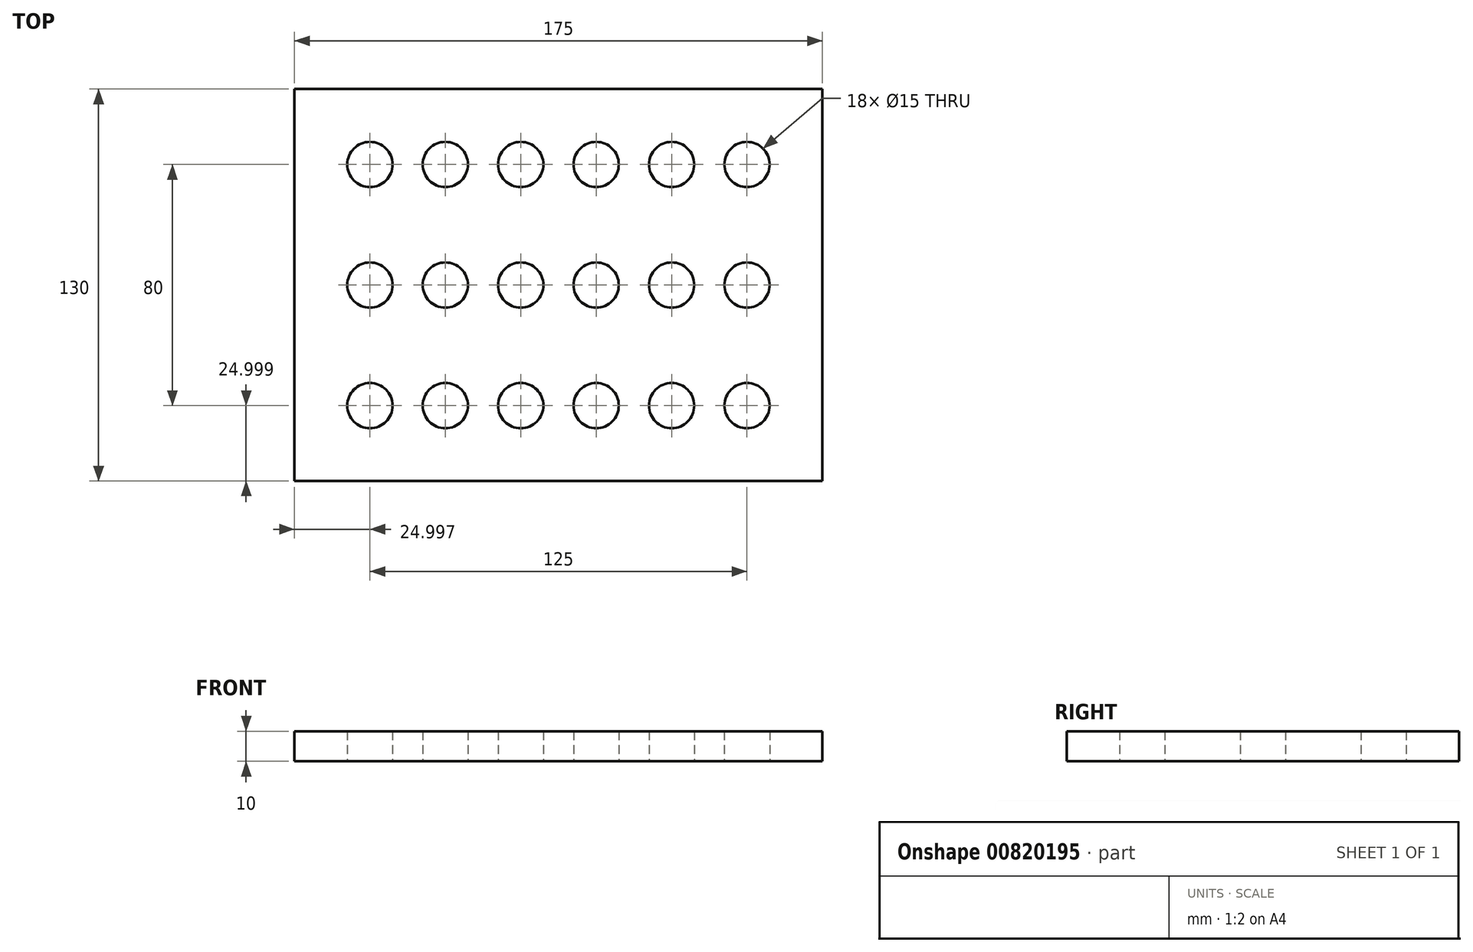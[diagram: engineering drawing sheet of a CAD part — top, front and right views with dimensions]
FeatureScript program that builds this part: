
annotation { "Feature Type Name" : "Feature", "Feature Type Description" : "" }
export const myFeature = defineFeature(function(context is Context, id is Id, definition is map)
    precondition{}
    {
        {
            var Q0;
            Q0=qCreatedBy(makeId("Top.planeOp"),FACE);
            var sketch = newSketch(context, id + "F0", { "sketchPlane" : qUnion([Q0])});
            skLineSegment(sketch, "E0.bottom", {"start": v(87.5, 65) * mm, "end": v(-87.5, 65) * mm});
            skLineSegment(sketch, "E0.top", {"start": v(87.5, -65) * mm, "end": v(-87.5, -65) * mm});
            skLineSegment(sketch, "E0.left", {"start": v(87.5, 65) * mm, "end": v(87.5, -65) * mm});
            skLineSegment(sketch, "E0.right", {"start": v(-87.5, 65) * mm, "end": v(-87.5, -65) * mm});
            skPoint(sketch, "E0.middle", {"position": v(0, 0) * mm});
            skCircle(sketch, "E1", {"center": v(-62.5, 40) * mm, "radius": 7.5 * mm});
            skLineSegment(sketch, "E2", {"start": v(-62.5, 40) * mm, "end": v(-87.5, 40) * mm, "construction": true});
            skLineSegment(sketch, "E3", {"start": v(-62.5, 40) * mm, "end": v(-62.5, 65) * mm, "construction": true});
            skCircle(sketch, "E4.0.1.0", {"center": v(-62.5, 0) * mm, "radius": 7.5 * mm});
            skCircle(sketch, "E4.0.2.0", {"center": v(-62.5, -40) * mm, "radius": 7.5 * mm});
            skCircle(sketch, "E4.1.0.0", {"center": v(-37.5, 40) * mm, "radius": 7.5 * mm});
            skCircle(sketch, "E4.1.1.0", {"center": v(-37.5, 0) * mm, "radius": 7.5 * mm});
            skCircle(sketch, "E4.1.2.0", {"center": v(-37.5, -40) * mm, "radius": 7.5 * mm});
            skCircle(sketch, "E4.2.0.0", {"center": v(-12.5, 40) * mm, "radius": 7.5 * mm});
            skCircle(sketch, "E4.2.1.0", {"center": v(-12.5, 0) * mm, "radius": 7.5 * mm});
            skCircle(sketch, "E4.2.2.0", {"center": v(-12.5, -40) * mm, "radius": 7.5 * mm});
            skCircle(sketch, "E4.3.0.0", {"center": v(12.5, 40) * mm, "radius": 7.5 * mm});
            skCircle(sketch, "E4.3.1.0", {"center": v(12.5, 0) * mm, "radius": 7.5 * mm});
            skCircle(sketch, "E4.3.2.0", {"center": v(12.5, -40) * mm, "radius": 7.5 * mm});
            skCircle(sketch, "E4.4.0.0", {"center": v(37.5, 40) * mm, "radius": 7.5 * mm});
            skCircle(sketch, "E4.4.1.0", {"center": v(37.5, 0) * mm, "radius": 7.5 * mm});
            skCircle(sketch, "E4.4.2.0", {"center": v(37.5, -40) * mm, "radius": 7.5 * mm});
            skCircle(sketch, "E4.5.0.0", {"center": v(62.5, 40) * mm, "radius": 7.5 * mm});
            skCircle(sketch, "E4.5.1.0", {"center": v(62.5, 0) * mm, "radius": 7.5 * mm});
            skCircle(sketch, "E4.5.2.0", {"center": v(62.5, -40) * mm, "radius": 7.5 * mm});
            skLineSegment(sketch, "E4.direction1", {"start": v(-62.5, 40) * mm, "end": v(-37.5, 40) * mm, "construction": true});
            skLineSegment(sketch, "E4.direction2", {"start": v(-62.5, 40) * mm, "end": v(-62.5, 0) * mm, "construction": true});
            skSolve(sketch);
        }
        {
            var Q0;
            Q0 = qSketchRegion(id + "F0", true);
            extrude(context, id + "F1", {"entities" : qUnion([Q0]), "depth" : 10 * mm, "offsetDistance" : 25.4 * mm});
        }
    });
